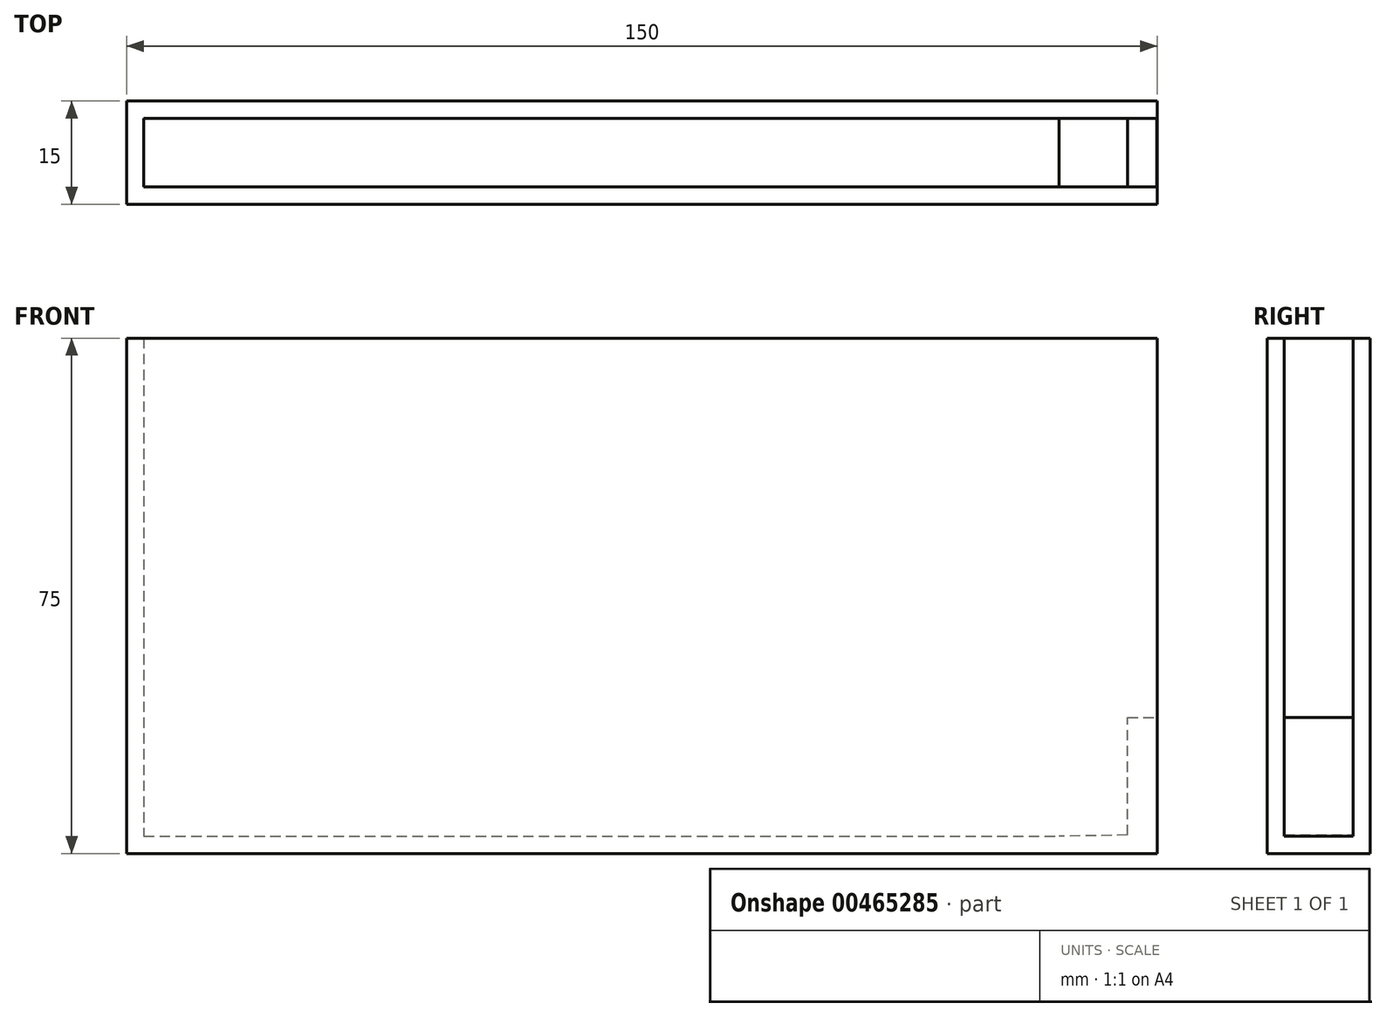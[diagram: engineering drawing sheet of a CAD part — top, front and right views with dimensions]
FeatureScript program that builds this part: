
annotation { "Feature Type Name" : "Feature", "Feature Type Description" : "" }
export const myFeature = defineFeature(function(context is Context, id is Id, definition is map)
    precondition{}
    {
        {
            var Q0;
            Q0=qCreatedBy(makeId("Front.planeOp"),FACE);
            var sketch = newSketch(context, id + "F0", { "sketchPlane" : qUnion([Q0])});
            skLineSegment(sketch, "E0.bottom", {"start": v(0, 0) * mm, "end": v(150, 0) * mm});
            skLineSegment(sketch, "E0.top", {"start": v(0, 75) * mm, "end": v(150, 75) * mm});
            skLineSegment(sketch, "E0.left", {"start": v(150, 75) * mm, "end": v(150, 0) * mm});
            skLineSegment(sketch, "E0.right", {"start": v(0, 75) * mm, "end": v(0, 0) * mm});
            skSolve(sketch);
        }
        {
            var Q0;
            Q0=makeQuery(id+"F0.imprint","IMPRINT",FACE,{"disambiguationData":[TD([[makeQuery(id+"F0.imprint","IMPRINT",EDGE,{"derivedFrom":sQuery(id+"F0.wireOp",EDGE,"E0.bottom")}),1.0]])]});
            extrude(context, id + "F1", {"entities" : qUnion([Q0]), "depth" : 15 * mm, "offsetDistance" : 25 * mm});
        }
        {
            var Q0;
            Q0=makeQuery(id+"F1.opExtrude","SWEPT_FACE",FACE,{"disambiguationData":[OSD([sQuery(id+"F0.wireOp",EDGE,"E0.top")])]});
            var Q1;
            Q1=makeQuery(id+"F1.opExtrude","SWEPT_FACE",FACE,{"disambiguationData":[OSD([sQuery(id+"F0.wireOp",EDGE,"E0.left")])]});
            shell(context, id + "F2", {"entities" : qUnion([Q0, Q1]), "thickness" : 2.5 * mm});
        }
        {
            var Q0;
            Q0=qCreatedBy(makeId("Front.planeOp"),FACE);
            var sketch = newSketch(context, id + "F3", { "sketchPlane" : qUnion([Q0])});
            skLineSegment(sketch, "E1", {"start": v(0, 0) * mm, "end": v(149.86, 2.76) * mm});
            skLineSegment(sketch, "E2", {"start": v(149.86, 2.76) * mm, "end": v(149.91, 0) * mm});
            skLineSegment(sketch, "E3", {"start": v(149.91, 0) * mm, "end": v(0, 0) * mm});
            skSolve(sketch);
        }
        {
            var Q0;
            Q0 = qSketchRegion(id + "F3", true);
            extrude(context, id + "F4", {"entities" : qUnion([Q0]), "depth" : 15 * mm, "offsetDistance" : 25 * mm});
        }
        {
            var Q0;
            Q0=makeQuery(id+"F0.imprint","IMPRINT",FACE,{"disambiguationData":[TD([[makeQuery(id+"F0.imprint","IMPRINT",EDGE,{"derivedFrom":sQuery(id+"F0.wireOp",EDGE,"E0.bottom")}),1.0]])]});
            var sketch = newSketch(context, id + "F5", { "sketchPlane" : qUnion([Q0])});
            skLineSegment(sketch, "E4.bottom", {"start": v(149.92, 0) * mm, "end": v(149.92, 0) * mm});
            skLineSegment(sketch, "E4.top", {"start": v(149.92, 19.82) * mm, "end": v(149.92, 19.82) * mm});
            skLineSegment(sketch, "E4.left", {"start": v(149.92, 0) * mm, "end": v(149.92, 19.82) * mm});
            skLineSegment(sketch, "E4.right", {"start": v(149.92, 0) * mm, "end": v(149.92, 19.82) * mm});
            skLineSegment(sketch, "E5.bottom", {"start": v(149.92, 19.82) * mm, "end": v(145.67, 19.82) * mm});
            skLineSegment(sketch, "E5.top", {"start": v(149.92, 19.82) * mm, "end": v(145.67, 19.82) * mm});
            skLineSegment(sketch, "E5.right", {"start": v(145.67, 19.82) * mm, "end": v(145.67, 19.82) * mm});
            skLineSegment(sketch, "E6.top", {"start": v(145.67, 0) * mm, "end": v(145.67, 0) * mm});
            skLineSegment(sketch, "E6.left", {"start": v(145.67, 19.82) * mm, "end": v(145.67, 0) * mm});
            skLineSegment(sketch, "E6.right", {"start": v(145.67, 19.82) * mm, "end": v(145.67, 0) * mm});
            skLineSegment(sketch, "E7.bottom", {"start": v(145.67, 0) * mm, "end": v(149.92, 0) * mm});
            skLineSegment(sketch, "E7.top", {"start": v(145.67, 0) * mm, "end": v(149.92, 0) * mm});
            skSolve(sketch);
        }
        {
            var Q0;
            Q0 = qSketchRegion(id + "F5", true);
            extrude(context, id + "F6", {"entities" : qUnion([Q0]), "operationType" : NewBodyOperationType.ADD, "depth" : 15 * mm, "offsetDistance" : 25 * mm});
        }
    });
